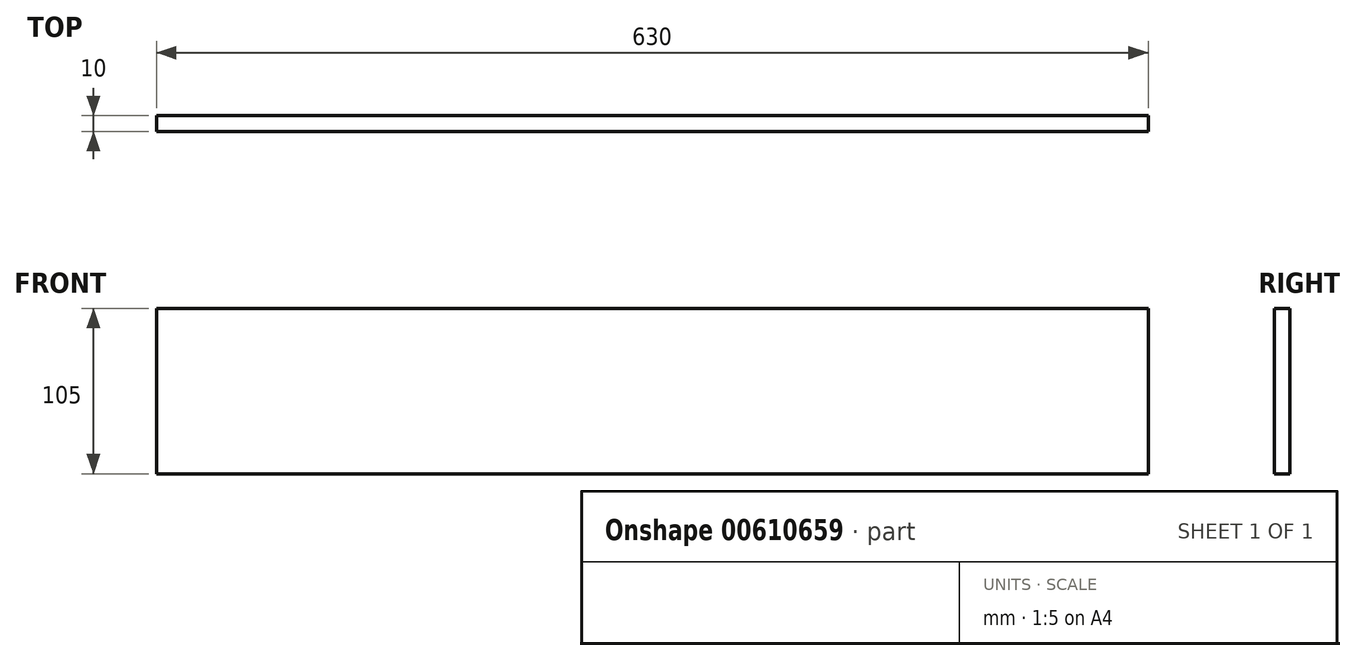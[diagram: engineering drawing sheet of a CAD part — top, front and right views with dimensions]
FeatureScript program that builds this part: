
annotation { "Feature Type Name" : "Feature", "Feature Type Description" : "" }
export const myFeature = defineFeature(function(context is Context, id is Id, definition is map)
    precondition{}
    {
        {
            var Q0;
            Q0=qCreatedBy(makeId("Front.planeOp"),FACE);
            var sketch = newSketch(context, id + "F0", { "sketchPlane" : qUnion([Q0])});
            skLineSegment(sketch, "E0.bottom", {"start": v(-279.26, -124.92) * mm, "end": v(350.74, -124.92) * mm});
            skLineSegment(sketch, "E0.top", {"start": v(-279.26, -229.92) * mm, "end": v(350.74, -229.92) * mm});
            skLineSegment(sketch, "E0.left", {"start": v(-279.26, -124.92) * mm, "end": v(-279.26, -229.92) * mm});
            skLineSegment(sketch, "E0.right", {"start": v(350.74, -124.92) * mm, "end": v(350.74, -229.92) * mm});
            skPoint(sketch, "E1.endSnap0", {"position": v(35.74, -124.92) * mm});
            skSolve(sketch);
        }
        {
            var Q0;
            Q0=makeQuery(id+"F0.imprint","IMPRINT",FACE,{"disambiguationData":[TD([[makeQuery(id+"F0.imprint","IMPRINT",EDGE,{"derivedFrom":sQuery(id+"F0.wireOp",EDGE,"E0.bottom")}),-1.0]])]});
            extrude(context, id + "F1", {"entities" : qUnion([Q0]), "depth" : 10 * mm, "offsetDistance" : 25 * mm});
        }
    });
